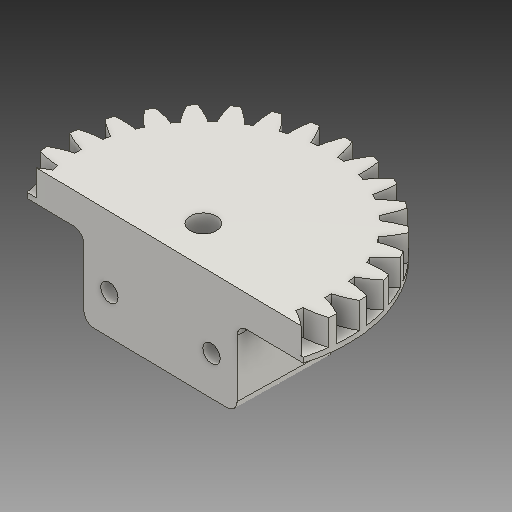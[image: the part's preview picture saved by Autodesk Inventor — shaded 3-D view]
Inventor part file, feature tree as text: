
AUTODESK INVENTOR PART (.ipt)
format: ipt  version: 2018 (Build 220112000, 112)  size: 322,048 bytes
history: native  units: mm
features: other x13, sketch x9, plane x4
ambient origin geometry x8: Origin, YZ Plane, XZ Plane, XY Plane, X Axis, Y Axis, Z Axis, Center Point
bodies: Volumenkörper1 (feature_tree)
feature tree (26):
  other  "Stirnzahnrad1"
  other  "Solid1::Stirnzahnrad1"
  other  "Bezeichnung1"
  sketch  "Sketch1"  dims[d0=10.0mm]
  sketch  "Sketch2"  dims[d16=40.0mm d17=0.0mm d41=0.0mm d43=40.0mm d46=40.0mm d47=0.0mm d48=0.0mm]
  sketch  "Skizze9"
  sketch  "Skizze10"
  sketch  "Skizze11"
  sketch  "Skizze12"
  sketch  "Skizze13"
  sketch  "Skizze14"
  sketch  "Skizze15"
  plane  "XZ Plane_1"
  plane  "Work Plane2"
  plane  "Work Plane8"
  plane  "Work Plane9"
  other  "Z Axis_1"
  other  "Flä1"
  other  "Srf1::Abgeleitet"
  other  "Abstands-iMate"
  other  "Ausrichtungs-iMate"
  other  "Netz-iMate"
  other  "Achsen-iMate"
  other  "Positions-iMate"
  other  "Netz-iMate 2"
  other  "Startebenen-iMate"
